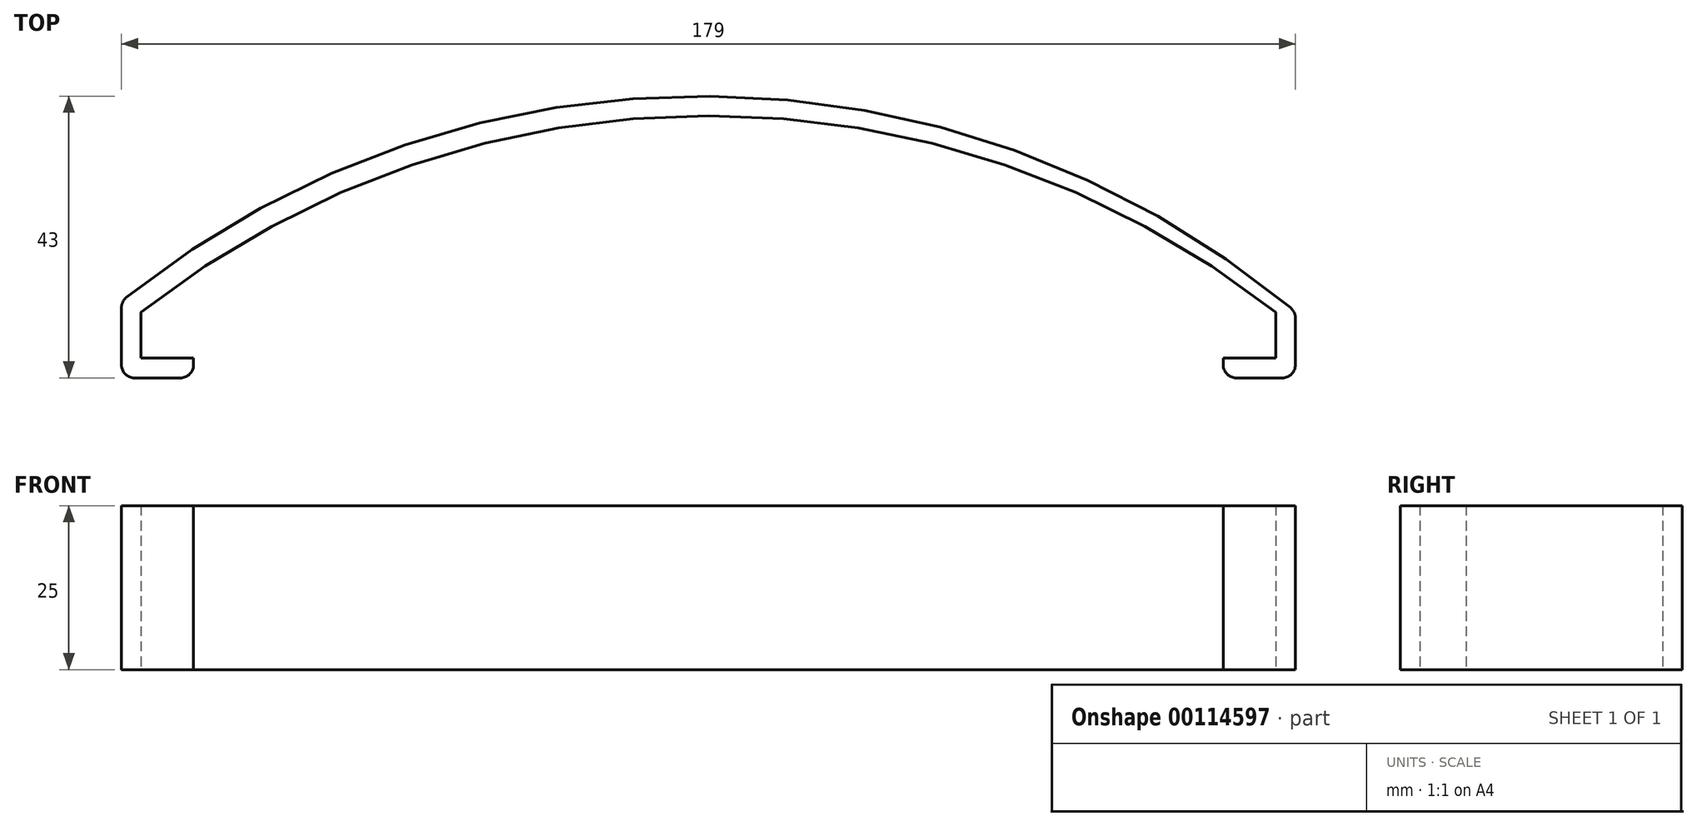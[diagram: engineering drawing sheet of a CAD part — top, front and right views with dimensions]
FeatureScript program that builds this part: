
annotation { "Feature Type Name" : "Feature", "Feature Type Description" : "" }
export const myFeature = defineFeature(function(context is Context, id is Id, definition is map)
    precondition{}
    {
        {
            var Q0;
            Q0=qCreatedBy(makeId("Top.planeOp"),FACE);
            var sketch = newSketch(context, id + "F0", { "sketchPlane" : qUnion([Q0])});
            skLineSegment(sketch, "E0", {"start": v(0, 0) * mm, "end": v(-8, 0) * mm});
            skLineSegment(sketch, "E1", {"start": v(-8, 0) * mm, "end": v(-8, 7) * mm});
            skLineSegment(sketch, "E2", {"start": v(-8, 7) * mm, "end": v(165, 7) * mm, "construction": true});
            skLineSegment(sketch, "E3", {"start": v(165, 7) * mm, "end": v(165, 0) * mm});
            skLineSegment(sketch, "E4", {"start": v(165, 0) * mm, "end": v(157, 0) * mm});
            skLineSegment(sketch, "E5", {"start": v(-8, 7) * mm, "end": v(78.5, 7) * mm});
            skLineSegment(sketch, "E6", {"start": v(78.5, 7) * mm, "end": v(78.5, 37) * mm, "construction": true});
            skArc(sketch, "E7", {"start": v(165, 7) * mm, "mid": v(78.5, 37) * mm, "end": v(-8, 7) * mm});
            skLineSegment(sketch, "E8", {"start": v(0, 0) * mm, "end": v(0, -1) * mm});
            skLineSegment(sketch, "E9", {"start": v(-2, -3) * mm, "end": v(-9, -3) * mm});
            skLineSegment(sketch, "E10", {"start": v(-11, -1) * mm, "end": v(-11, 7.71) * mm});
            skLineSegment(sketch, "E11", {"start": v(157, 0) * mm, "end": v(157, -1) * mm});
            skLineSegment(sketch, "E12", {"start": v(159, -3) * mm, "end": v(166, -3) * mm});
            skLineSegment(sketch, "E13", {"start": v(168, -1) * mm, "end": v(168, 6.14) * mm});
            skLineSegment(sketch, "E14", {"start": v(78.5, 37) * mm, "end": v(78.5, 40) * mm, "construction": true});
            skArc(sketch, "E15", {"start": v(167.28, 7.69) * mm, "mid": v(78.8, 40) * mm, "end": v(-10.25, 9.27) * mm});
            skPoint(sketch, "E16.visualSharp", {"position": v(-11, -3) * mm});
            skArc(sketch, "E16.filletArc", {"start": v(-11, -1) * mm, "mid": v(-10.41, -2.41) * mm, "end": v(-9, -3) * mm});
            skPoint(sketch, "E17.visualSharp", {"position": v(0, -3) * mm});
            skArc(sketch, "E17.filletArc", {"start": v(-2, -3) * mm, "mid": v(-0.59, -2.41) * mm, "end": v(0, -1) * mm});
            skPoint(sketch, "E18.visualSharp", {"position": v(157, -3) * mm});
            skArc(sketch, "E18.filletArc", {"start": v(157, -1) * mm, "mid": v(157.59, -2.41) * mm, "end": v(159, -3) * mm});
            skPoint(sketch, "E19.visualSharp", {"position": v(168, -3) * mm});
            skArc(sketch, "E19.filletArc", {"start": v(166, -3) * mm, "mid": v(167.41, -2.41) * mm, "end": v(168, -1) * mm});
            skPoint(sketch, "E20.visualSharp", {"position": v(168, 7.08) * mm});
            skArc(sketch, "E20.filletArc", {"start": v(168, 6.14) * mm, "mid": v(167.8, 7) * mm, "end": v(167.28, 7.69) * mm});
            skPoint(sketch, "E21.visualSharp", {"position": v(-11, 8.67) * mm});
            skArc(sketch, "E21.filletArc", {"start": v(-10.25, 9.27) * mm, "mid": v(-10.8, 8.58) * mm, "end": v(-11, 7.71) * mm});
            skSolve(sketch);
        }
        {
            var Q0;
            Q0 = qSketchRegion(id + "F0", true);
            extrude(context, id + "F1", {"entities" : qUnion([Q0]), "depth" : 25 * mm});
        }
    });
